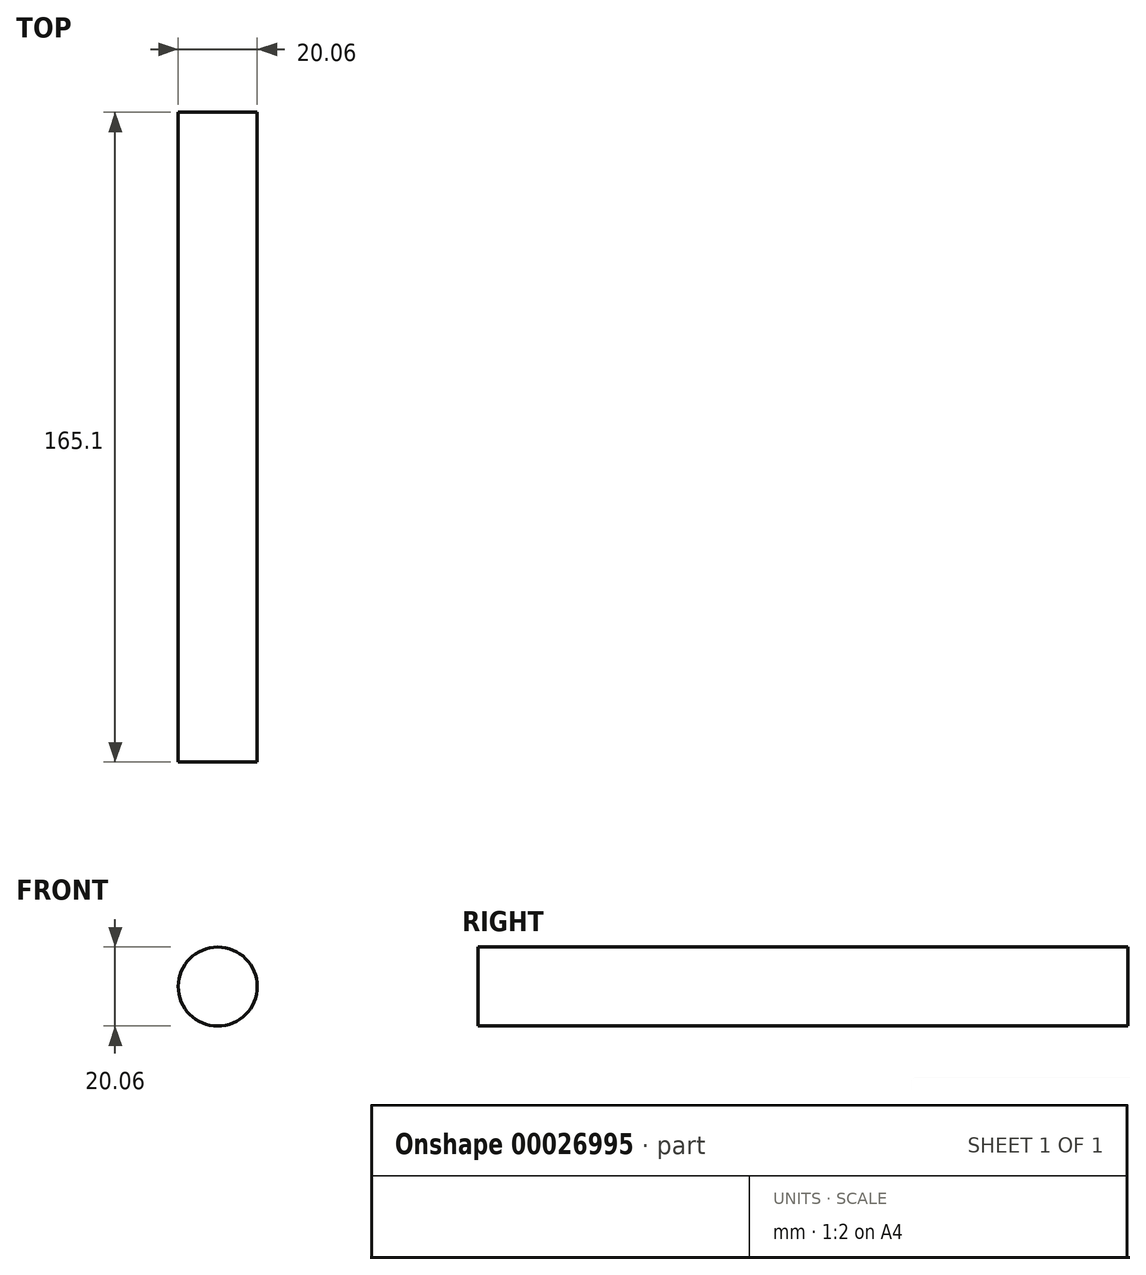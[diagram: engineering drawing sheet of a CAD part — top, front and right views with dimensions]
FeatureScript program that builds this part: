
annotation { "Feature Type Name" : "Feature", "Feature Type Description" : "" }
export const myFeature = defineFeature(function(context is Context, id is Id, definition is map)
    precondition{}
    {
        {
            var Q0;
            Q0=qCreatedBy(makeId("Front.planeOp"),FACE);
            var sketch = newSketch(context, id + "F0", { "sketchPlane" : qUnion([Q0])});
            skCircle(sketch, "E0", {"center": v(0, -0.5) * mm, "radius": 10.03 * mm});
            skSolve(sketch);
        }
        {
            var Q0;
            Q0=makeQuery(id+"F0.imprint","IMPRINT",FACE,{"disambiguationData":[TD([[makeQuery(id+"F0.imprint","IMPRINT",EDGE,{"derivedFrom":sQuery(id+"F0.wireOp",EDGE,"E0")}),1.0]])]});
            extrude(context, id + "F1", {"entities" : qUnion([Q0]), "depth" : 165.1 * mm});
        }
    });
